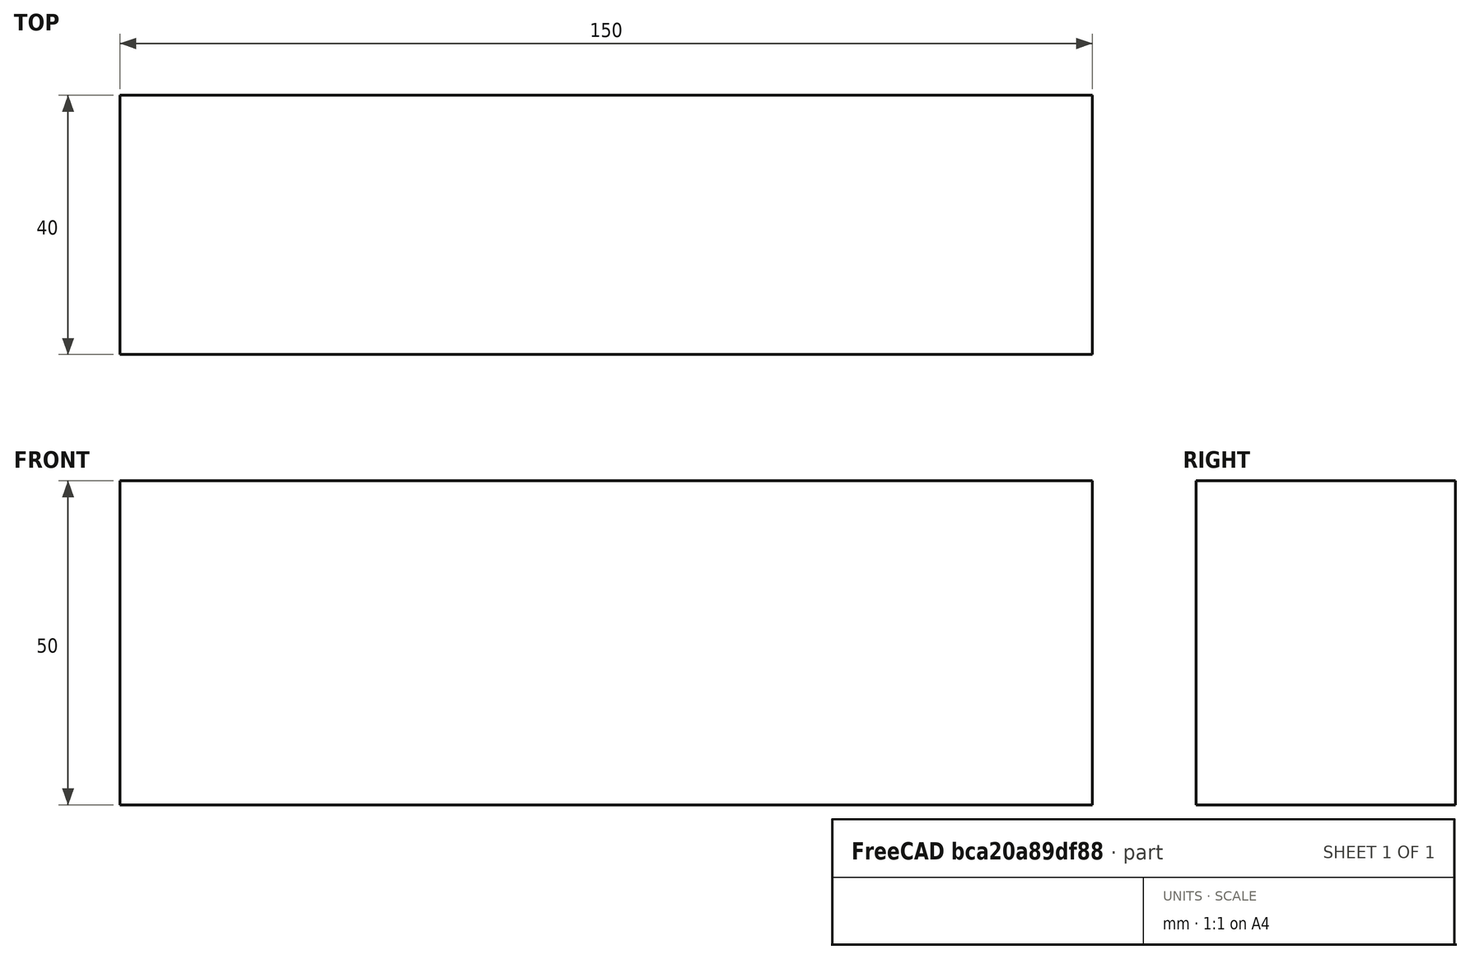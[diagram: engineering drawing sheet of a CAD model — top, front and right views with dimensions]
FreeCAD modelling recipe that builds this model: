
FCSTD DOCUMENT  (FreeCAD 0.15R4671 (Git))
Label: Flat Bar 150x40 EN10058 S235JR
License: All rights reserved
LicenseURL: http://en.wikipedia.org/wiki/All_rights_reserved
objects: Sketcher::SketchObject×1, Part::Extrusion×1
note: 2 computed .brp shape members not serialized (recipe doc carries the construction recipe); baked Part::Feature solids carry a one-line shape summary decoded from their .brp

FEATURE [Sketcher::SketchObject] Sketch
  sketch-geometry (4):
    g0: LineSegment StartX=-75 StartY=-20 StartZ=0 EndX=75 EndY=-20 EndZ=0
    g1: LineSegment StartX=75 StartY=-20 StartZ=0 EndX=75 EndY=20 EndZ=0
    g2: LineSegment StartX=75 StartY=20 StartZ=0 EndX=-75 EndY=20 EndZ=0
    g3: LineSegment StartX=-75 StartY=20 StartZ=0 EndX=-75 EndY=-20 EndZ=0
  constraints (12):
    c: Coincident(g0,g1)
    c: Coincident(g1,g2)
    c: Coincident(g2,g3)
    c: Coincident(g3,g0)
    c: Horizontal(g0)
    c: Horizontal(g2)
    c: Vertical(g1)
    c: Vertical(g3)
    c: Symmetric(g1,g2,g-2)
    c: Symmetric(g0,g1,g-1)
    c: DistanceY(g1) = 40
    c: DistanceX(g0) = 150
FEATURE [Part::Extrusion] Extrude  label="Flat Bar 150x40 EN10058 S235JR"
  Base = -> Sketch
  Dir = (0,0,50)
  Solid = true
